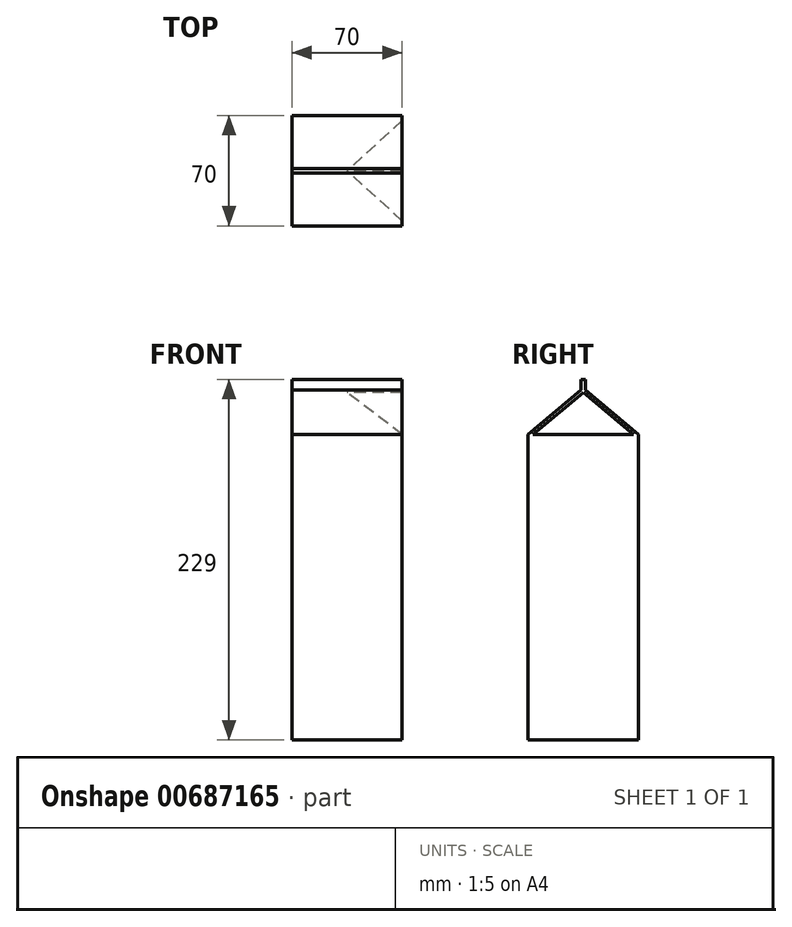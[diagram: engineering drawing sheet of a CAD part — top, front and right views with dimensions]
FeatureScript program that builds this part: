
annotation { "Feature Type Name" : "Feature", "Feature Type Description" : "" }
export const myFeature = defineFeature(function(context is Context, id is Id, definition is map)
    precondition{}
    {
        {
            var Q0;
            Q0=qCreatedBy(makeId("Right.planeOp"),FACE);
            var sketch = newSketch(context, id + "F0", { "sketchPlane" : qUnion([Q0])});
            skLineSegment(sketch, "E0", {"start": v(0, 0) * mm, "end": v(0, 194) * mm});
            skLineSegment(sketch, "E1", {"start": v(0, 194) * mm, "end": v(33.5, 222.1) * mm});
            skLineSegment(sketch, "E2", {"start": v(33.5, 222.1) * mm, "end": v(33.5, 229) * mm});
            skLineSegment(sketch, "E3", {"start": v(33.5, 229) * mm, "end": v(36.5, 229) * mm});
            skLineSegment(sketch, "E4", {"start": v(36.5, 229) * mm, "end": v(36.5, 222.1) * mm});
            skLineSegment(sketch, "E5", {"start": v(36.5, 222.1) * mm, "end": v(70, 194) * mm});
            skLineSegment(sketch, "E6", {"start": v(70, 194) * mm, "end": v(70, 0) * mm});
            skLineSegment(sketch, "E7", {"start": v(70, 0) * mm, "end": v(0, 0) * mm});
            skSolve(sketch);
        }
        {
            var Q0;
            Q0=makeQuery(id+"F0.imprint","IMPRINT",FACE,{"disambiguationData":[TD([[makeQuery(id+"F0.imprint","IMPRINT",EDGE,{"derivedFrom":sQuery(id+"F0.wireOp",EDGE,"E0")}),-1.0]])]});
            extrude(context, id + "F1", {"entities" : qUnion([Q0]), "depth" : 70 * mm, "offsetDistance" : 25 * mm});
        }
        {
            var Q0;
            Q0=makeQuery(id+"F1.opExtrude","CAP_FACE",FACE,{"disambiguationData":[OSD([sQuery(id+"F0.wireOp",EDGE,"E0"),sQuery(id+"F0.wireOp",EDGE,"E1"),sQuery(id+"F0.wireOp",EDGE,"E2"),sQuery(id+"F0.wireOp",EDGE,"E3"),sQuery(id+"F0.wireOp",EDGE,"E4"),sQuery(id+"F0.wireOp",EDGE,"E5"),sQuery(id+"F0.wireOp",EDGE,"E6"),sQuery(id+"F0.wireOp",EDGE,"E7")])],"isStart":false});
            var sketch = newSketch(context, id + "F2", { "sketchPlane" : qUnion([Q0])});
            skLineSegment(sketch, "E8", {"start": v(3.11, 194) * mm, "end": v(66.89, 194) * mm});
            skLineSegment(sketch, "E9", {"start": v(66.89, 194) * mm, "end": v(35, 220.76) * mm});
            skLineSegment(sketch, "E10", {"start": v(35, 220.76) * mm, "end": v(3.11, 194) * mm});
            skSolve(sketch);
        }
        {
            var Q0;
            Q0=qCreatedBy(makeId("Right.planeOp"),FACE);
            cPlane(context, id + "F3", {"entities" : qUnion([Q0]), "cplaneType" : CPlaneType.OFFSET, "offset" : 35 * mm, "width" : 150 * mm, "height" : 150 * mm});
        }
        {
            var Q0;
            Q0=qCreatedBy(id+"F3.planeOp",FACE);
            var sketch = newSketch(context, id + "F4", { "sketchPlane" : qUnion([Q0])});
            skPoint(sketch, "E11", {"position": v(35, 220.76) * mm});
            skSolve(sketch);
        }
        {
            var Q1;
            Q1=makeQuery(id+"F2.imprint","IMPRINT",FACE,{"disambiguationData":[TD([[makeQuery(id+"F2.imprint","IMPRINT",EDGE,{"derivedFrom":sQuery(id+"F2.wireOp",EDGE,"E8")}),1.0]])]});
            var Q2;
            Q2=sQuery(id+"F4.wireOp",VERTEX,"E11");
            loft(context, id + "F5", {"operationType" : NewBodyOperationType.REMOVE, "sheetProfilesArray" : [{ "sheetProfileEntities" : qUnion([Q1]) }, { "sheetProfileEntities" : qUnion([Q2]) }]});
        }
    });
